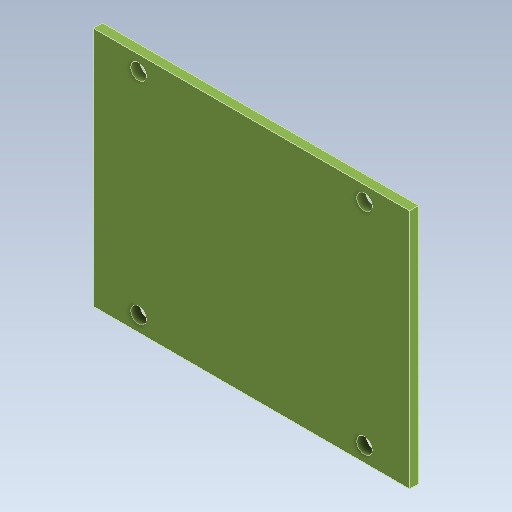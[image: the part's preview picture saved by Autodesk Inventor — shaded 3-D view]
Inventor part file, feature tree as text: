
AUTODESK INVENTOR PART (.ipt)
format: ipt  version: 2021 (Build 250183000, 183)  size: 103,936 bytes
history: native  units: mm
features: sketch x1, extrude x1, hole x1
ambient origin geometry x8: Origin, YZ Plane, XZ Plane, XY Plane, X Axis, Y Axis, Z Axis, Center Point
bodies: Solid1 (feature_tree)
feature tree (3):
  sketch  "Sketch1"  dims[d0=63.0mm d1=48.0mm d2=45.0mm d3=42.0mm d4=3.0mm d5=9.0mm d6=9.0mm d7=3.0mm d8=1.8mm d9=0.0mm d10=3.1mm d11=6.0mm d12=4.0mm d13=2.0mm d14=90.0deg d15=7.0mm d16=0.0mm]
  extrude  "Extrusion1"  Depth=48.0mm
  hole  "Hole1"  [1 undecoded]
note: 1 required parameter value undecoded (feature->parameter linkage not recoverable at this tier; creation-order binding heuristic only, values carry confidence <= 0.55)
